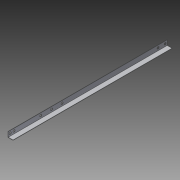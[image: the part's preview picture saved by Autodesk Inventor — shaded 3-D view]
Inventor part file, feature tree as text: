
AUTODESK INVENTOR PART (.ipt)
format: ipt  version: 2014 SP1 (Build 180222100, 222)  size: 127,488 bytes
history: native  units: in
note: dims shown in document units (in); Inventor stores cm internally (conversion verified against a paired STEP export)
features: extrude x2, sketch x2, reference x1
ambient origin geometry x8: Origin, YZ Plane, XZ Plane, XY Plane, X Axis, Y Axis, Z Axis, Center Point
bodies: Solid1 (feature_tree)
feature tree (5):
  extrude  "Extrusion1"  Depth=0.0312in
  extrude  "Extrusion2"  TaperAngle=0.0deg  [1 undecoded]
  sketch  "Sketch1"  dims[d0=0.625in d1=0.0312in]
  sketch  "Sketch2"  dims[d2=19.5in d3=0.0in d4=0.0in d5=0.0in]
  reference  "Reference1"
note: 1 required parameter value undecoded (feature->parameter linkage not recoverable at this tier; creation-order binding heuristic only, values carry confidence <= 0.55)
